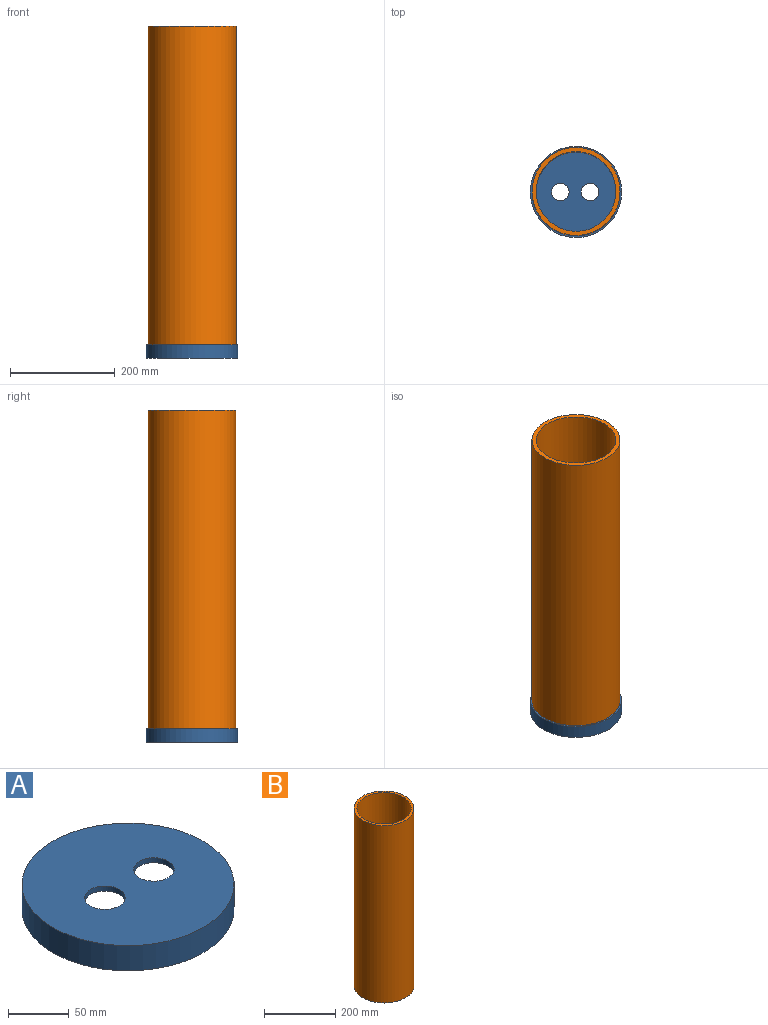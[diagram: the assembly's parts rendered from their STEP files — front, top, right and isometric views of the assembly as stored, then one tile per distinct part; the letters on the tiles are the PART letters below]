
ASSEMBLY  parts=2 mates=1
PART A: 7 faces, bbox 174.5x174.5x25.4 mm
  f0: cylinder r=87.27mm len=174.55mm, axis (0,0,-1), area 13928.3mm2, adj f1,f2
  f1: plane 174.55x174.55mm, normal (0,0,1), area 22173.7mm2, adj f0,f5,f6
  f2: plane 174.55x174.55mm, normal (0,0,-1), area 4008.6mm2, adj f0,f3
  f3: cylinder r=79.63mm len=159.26mm, axis (0,0,1), area 10166.6mm2, adj f2,f4
  f4: plane 159.26x159.26mm, normal (0,0,-1), area 18165.1mm2, adj f3,f5,f6
  f5: cylinder r=16.71mm len=33.43mm, axis (0,0,1), area 533.5mm2, adj f1,f4
  f6: cylinder r=16.71mm len=33.43mm, axis (0,0,1), area 533.5mm2, adj f1,f4
PART B: 4 faces, bbox 168.3x168.3x609.6 mm
  f0: cylinder r=76.2mm len=609.6mm, axis (0,0,-1), area 291863.5mm2, adj f2,f3
  f1: cylinder r=84.14mm len=609.6mm, axis (0,0,-1), area 322266mm2, adj f2,f3
  f2: plane 168.28x168.28mm, normal (0,0,1), area 3998.2mm2, adj f0,f1
  f3: plane 168.28x168.28mm, normal (0,0,-1), area 3998.2mm2, adj f0,f1
PLACE A rot(axis=(0,1,0),180deg) t=(230.68,-457.51,-190.62)mm
PLACE B t=(230.68,-457.51,-190.62)mm
MATE fastened B.f0 <-> A.f3  axis (0,0,-1) through (230.68,-457.51,-190.62)mm
